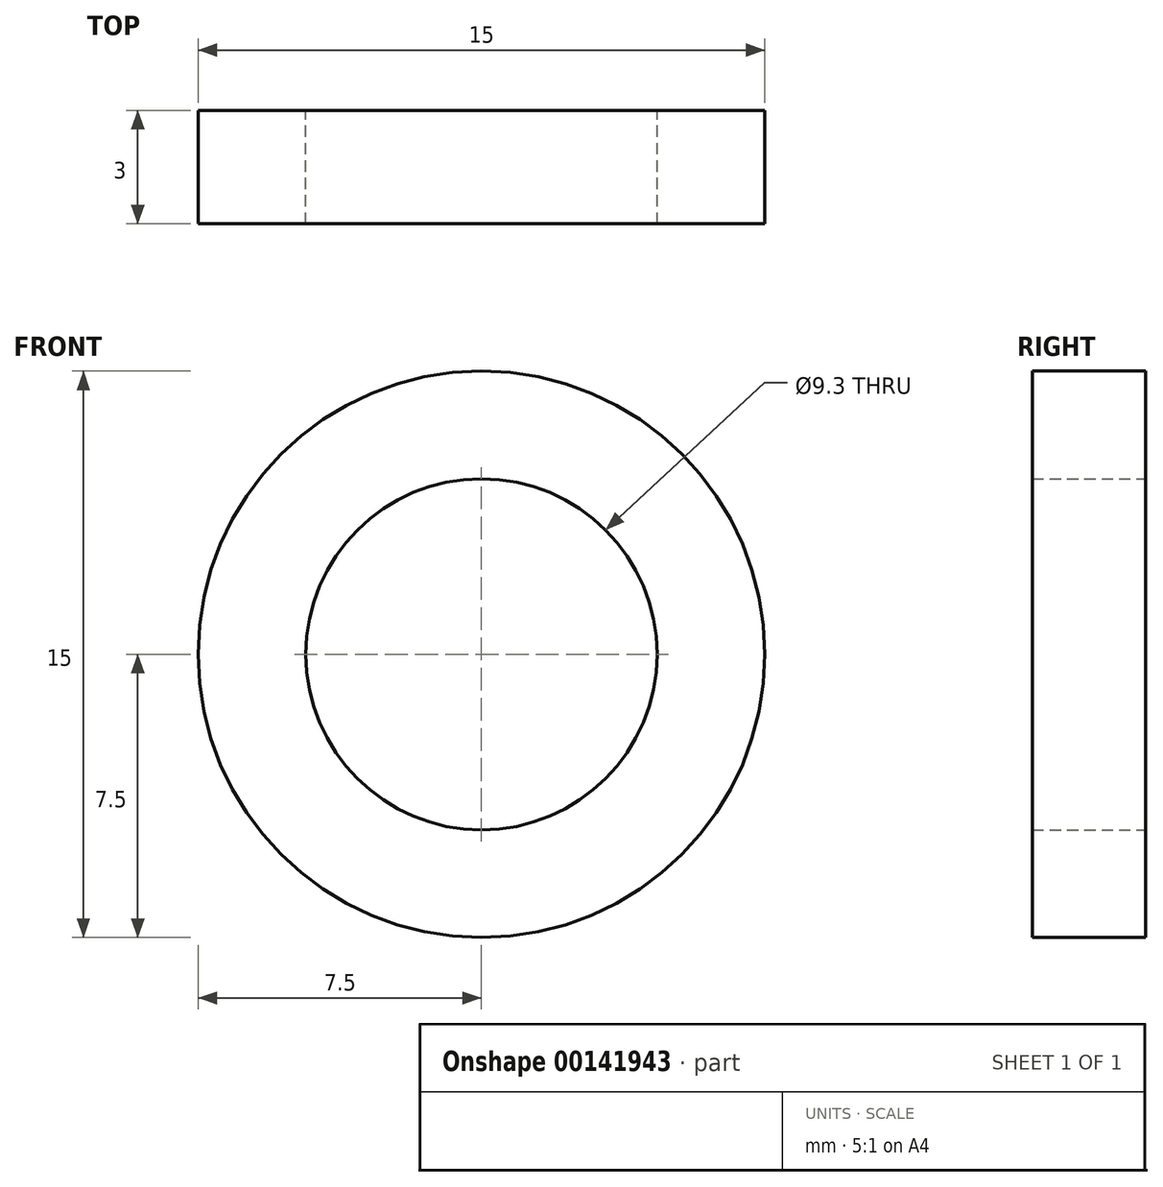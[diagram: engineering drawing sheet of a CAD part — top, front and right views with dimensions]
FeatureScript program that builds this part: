
annotation { "Feature Type Name" : "Feature", "Feature Type Description" : "" }
export const myFeature = defineFeature(function(context is Context, id is Id, definition is map)
    precondition{}
    {
        {
            var Q0;
            Q0=qCreatedBy(makeId("Front.planeOp"),FACE);
            var sketch = newSketch(context, id + "F0", { "sketchPlane" : qUnion([Q0])});
            skCircle(sketch, "E0", {"center": v(0, 0) * mm, "radius": 4.65 * mm});
            skCircle(sketch, "E1", {"center": v(0, 0) * mm, "radius": 7.5 * mm});
            skSolve(sketch);
        }
        {
            var Q0;
            Q0=makeQuery(id+"F0.imprint","IMPRINT",FACE,{"disambiguationData":[TD([[makeQuery(id+"F0.imprint","IMPRINT",EDGE,{"derivedFrom":sQuery(id+"F0.wireOp",EDGE,"E0")}),-1.0]])]});
            extrude(context, id + "F1", {"entities" : qUnion([Q0]), "depth" : 3 * mm, "offsetDistance" : 25 * mm});
        }
    });
